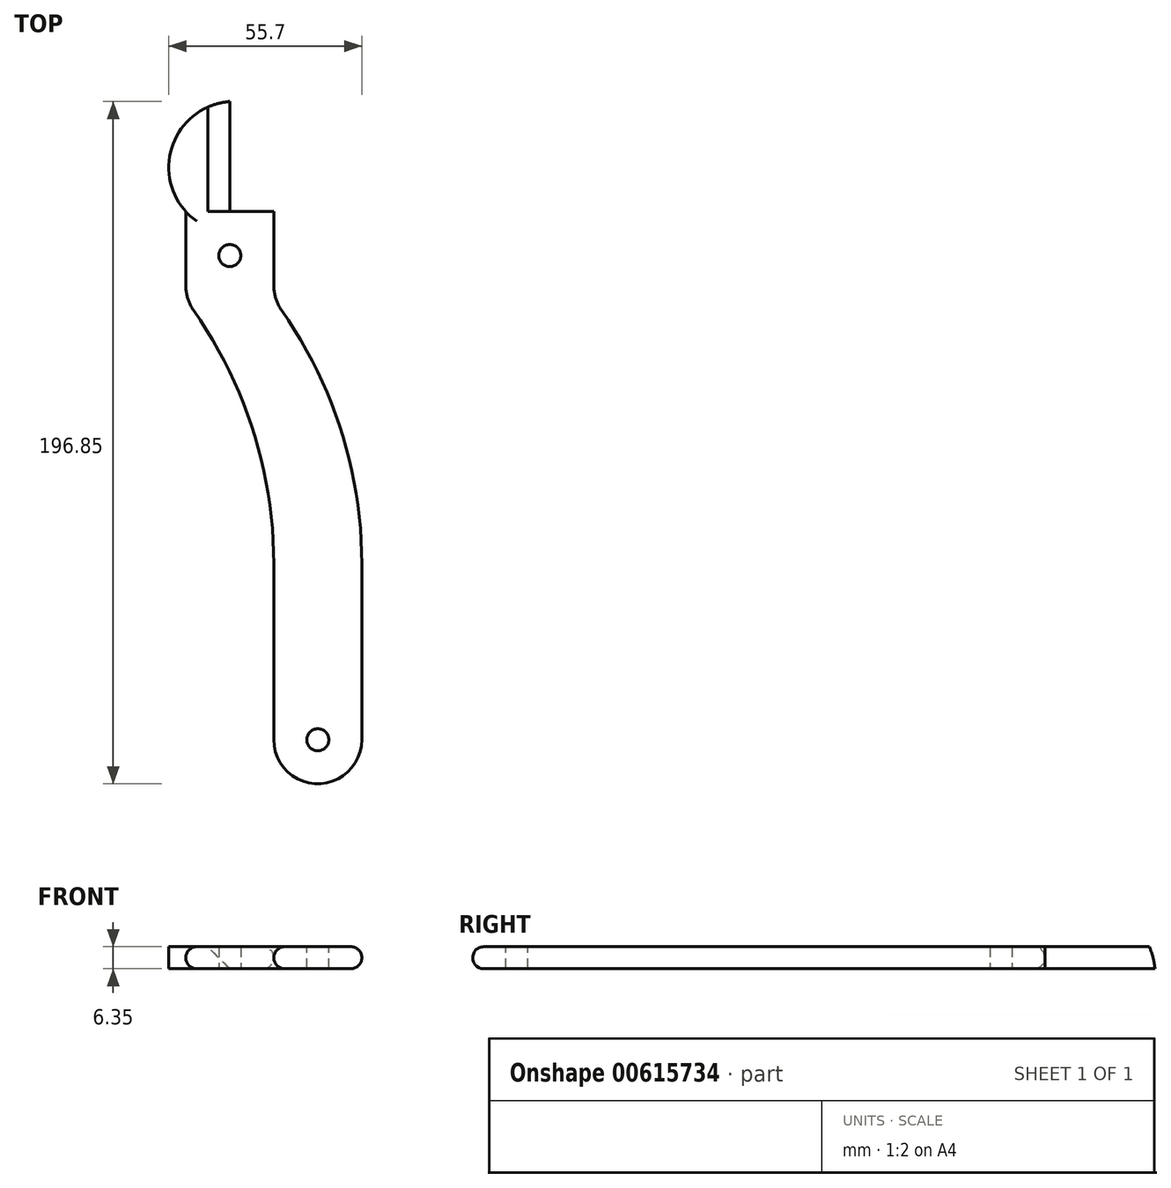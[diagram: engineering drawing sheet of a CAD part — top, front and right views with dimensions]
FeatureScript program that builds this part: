
annotation { "Feature Type Name" : "Feature", "Feature Type Description" : "" }
export const myFeature = defineFeature(function(context is Context, id is Id, definition is map)
    precondition{}
    {
        {
            var Q0;
            Q0=qCreatedBy(makeId("Top.planeOp"),FACE);
            var sketch = newSketch(context, id + "F0", { "sketchPlane" : qUnion([Q0])});
            skArc(sketch, "E0", {"start": v(-23.04, -20.27) * mm, "mid": v(-10.34, -32.97) * mm, "end": v(2.36, -20.27) * mm});
            skLineSegment(sketch, "E1", {"start": v(2.36, -20.27) * mm, "end": v(2.36, 30.53) * mm});
            skLineSegment(sketch, "E2", {"start": v(-23.04, -20.27) * mm, "end": v(-23.04, 30.53) * mm});
            skArc(sketch, "E3", {"start": v(2.36, 30.53) * mm, "mid": v(-3.55, 68.82) * mm, "end": v(-20.73, 103.55) * mm});
            skArc(sketch, "E4", {"start": v(-23.04, 30.53) * mm, "mid": v(-28.95, 68.82) * mm, "end": v(-46.13, 103.55) * mm});
            skLineSegment(sketch, "E5", {"start": v(-48.44, 110.85) * mm, "end": v(-48.44, 132.13) * mm});
            skLineSegment(sketch, "E6", {"start": v(-23.04, 110.85) * mm, "end": v(-23.04, 132.13) * mm});
            skPoint(sketch, "E7.visualSharp", {"position": v(-48.44, 106.73) * mm});
            skArc(sketch, "E7.filletArc", {"start": v(-48.44, 110.85) * mm, "mid": v(-47.85, 107.03) * mm, "end": v(-46.13, 103.55) * mm});
            skPoint(sketch, "E8.visualSharp", {"position": v(-23.04, 106.73) * mm});
            skArc(sketch, "E8.filletArc", {"start": v(-23.04, 110.85) * mm, "mid": v(-22.45, 107.03) * mm, "end": v(-20.73, 103.55) * mm});
            skLineSegment(sketch, "E9", {"start": v(-23.04, 132.13) * mm, "end": v(-35.74, 132.13) * mm});
            skLineSegment(sketch, "E10", {"start": v(-35.74, 132.13) * mm, "end": v(-35.74, 163.88) * mm});
            skArc(sketch, "E11", {"start": v(-35.74, 163.88) * mm, "mid": v(-51.98, 151.96) * mm, "end": v(-48.44, 132.13) * mm});
            skCircle(sketch, "E12", {"center": v(-35.74, 119.43) * mm, "radius": 3.18 * mm});
            skSolve(sketch);
        }
        {
            var Q0;
            Q0 = qSketchRegion(id + "F0", true);
            extrude(context, id + "F1", {"entities" : qUnion([Q0]), "depth" : 6.35 * mm, "offsetDistance" : 25.4 * mm});
        }
        {
            var Q0;
            Q0=makeQuery(id+"F1.opExtrude","CAP_EDGE",EDGE,{"disambiguationData":[OSD([sQuery(id+"F0.wireOp",EDGE,"E10")])],"isStart":false});
            chamfer(context, id + "F2", {"entities" : qUnion([Q0]), "width" : 6.35 * mm, "tangentPropagation" : true});
        }
        {
            var Q0;
            Q0=makeQuery(id+"F1.opExtrude","CAP_EDGE",EDGE,{"disambiguationData":[OSD([sQuery(id+"F0.wireOp",EDGE,"E4")])],"isStart":false});
            var Q1;
            Q1=makeQuery(id+"F1.opExtrude","CAP_EDGE",EDGE,{"disambiguationData":[OSD([sQuery(id+"F0.wireOp",EDGE,"E4")])],"isStart":true});
            fillet(context, id + "F3", {"entities" : qUnion([Q0, Q1]), "radius" : 3.17 * mm, "tangentPropagation" : true, "allowEdgeOverflow" : false});
        }
        {
            var Q0;
            Q0=makeQuery(id+"F1.opExtrude","CAP_FACE",FACE,{"disambiguationData":[OSD([sQuery(id+"F0.wireOp",EDGE,"E0"),sQuery(id+"F0.wireOp",EDGE,"E1"),sQuery(id+"F0.wireOp",EDGE,"E2"),sQuery(id+"F0.wireOp",EDGE,"E3"),sQuery(id+"F0.wireOp",EDGE,"E4"),sQuery(id+"F0.wireOp",EDGE,"E5"),sQuery(id+"F0.wireOp",EDGE,"E6"),sQuery(id+"F0.wireOp",EDGE,"E7.filletArc"),sQuery(id+"F0.wireOp",EDGE,"E8.filletArc"),sQuery(id+"F0.wireOp",EDGE,"E9"),sQuery(id+"F0.wireOp",EDGE,"E10"),sQuery(id+"F0.wireOp",EDGE,"E11"),sQuery(id+"F0.wireOp",EDGE,"E12")])],"isStart":false});
            var sketch = newSketch(context, id + "F4", { "sketchPlane" : qUnion([Q0])});
            skCircle(sketch, "E13", {"center": v(-10.34, -20.27) * mm, "radius": 3.18 * mm});
            skSolve(sketch);
        }
        {
            var Q0;
            Q0 = qSketchRegion(id + "F4", true);
            extrude(context, id + "F5", {"entities" : qUnion([Q0]), "operationType" : NewBodyOperationType.REMOVE, "oppositeDirection" : true, "depth" : 6.35 * mm, "offsetDistance" : 25.4 * mm});
        }
    });
